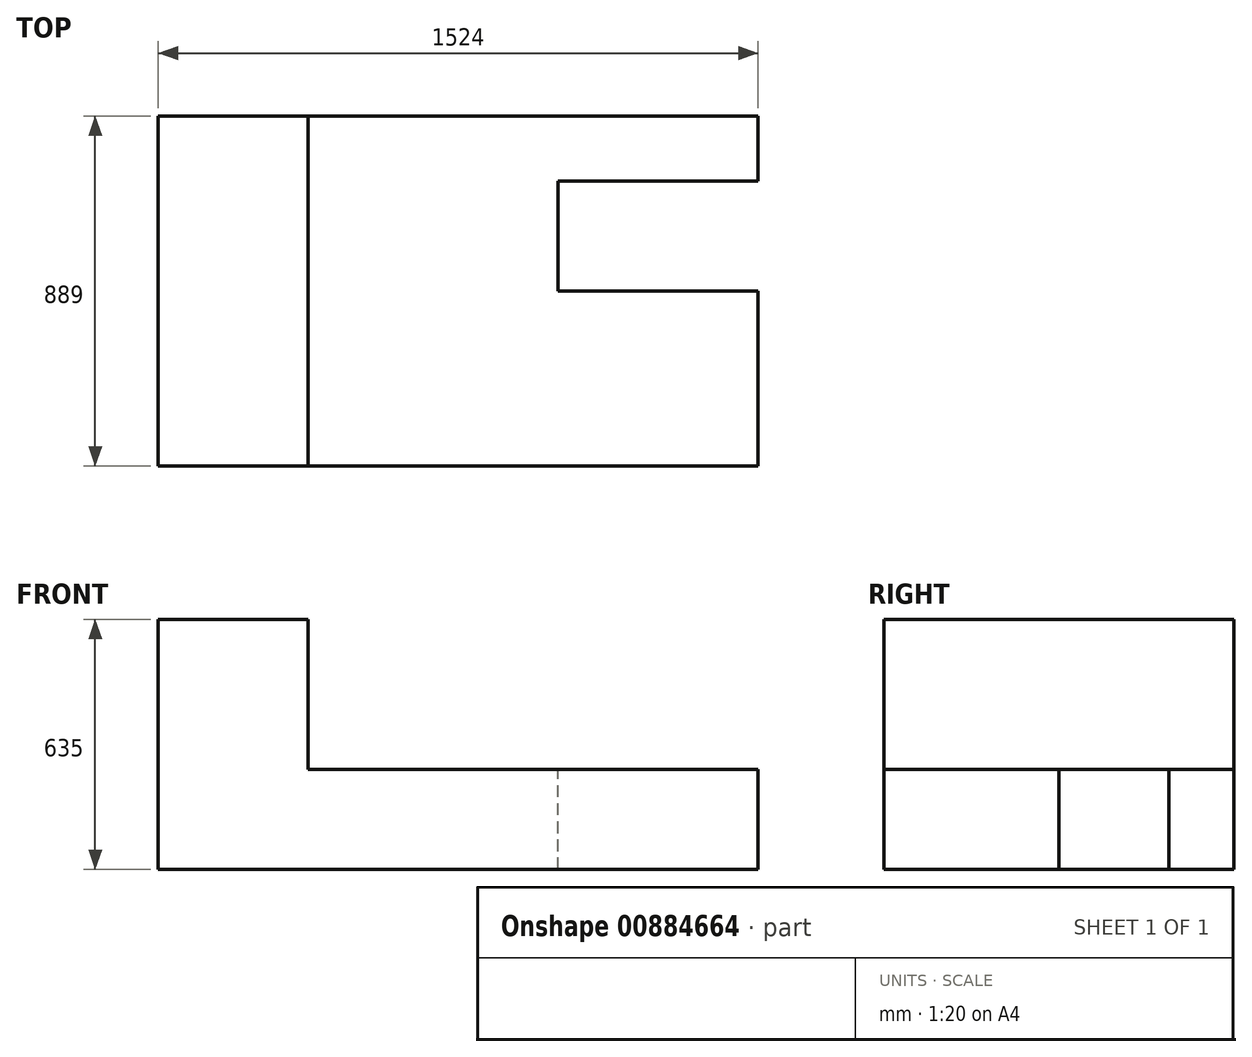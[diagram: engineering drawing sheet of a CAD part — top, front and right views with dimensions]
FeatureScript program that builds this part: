
annotation { "Feature Type Name" : "Feature", "Feature Type Description" : "" }
export const myFeature = defineFeature(function(context is Context, id is Id, definition is map)
    precondition{}
    {
        {
            var Q0;
            Q0=qCreatedBy(makeId("Front.planeOp"),FACE);
            var sketch = newSketch(context, id + "F0", { "sketchPlane" : qUnion([Q0])});
            skLineSegment(sketch, "E0", {"start": v(0, 0) * mm, "end": v(1524, 0) * mm});
            skLineSegment(sketch, "E1", {"start": v(1524, 0) * mm, "end": v(1524, 254) * mm});
            skLineSegment(sketch, "E2", {"start": v(1524, 254) * mm, "end": v(381, 254) * mm});
            skLineSegment(sketch, "E3", {"start": v(381, 254) * mm, "end": v(381, 635) * mm});
            skLineSegment(sketch, "E4", {"start": v(381, 635) * mm, "end": v(0, 635) * mm});
            skLineSegment(sketch, "E5", {"start": v(0, 635) * mm, "end": v(0, 0) * mm});
            skSolve(sketch);
        }
        {
            var Q0;
            Q0=makeQuery(id+"F0.imprint","IMPRINT",FACE,{"disambiguationData":[TD([[makeQuery(id+"F0.imprint","IMPRINT",EDGE,{"derivedFrom":sQuery(id+"F0.wireOp",EDGE,"E0")}),1.0]])]});
            extrude(context, id + "F1", {"entities" : qUnion([Q0]), "depth" : 889 * mm, "offsetDistance" : 25.4 * mm});
        }
        {
            var Q0;
            Q0=makeQuery(id+"F1.opExtrude","SWEPT_FACE",FACE,{"disambiguationData":[OSD([sQuery(id+"F0.wireOp",EDGE,"E2")])]});
            var sketch = newSketch(context, id + "F2", { "sketchPlane" : qUnion([Q0])});
            skLineSegment(sketch, "E6", {"start": v(1524, -444.5) * mm, "end": v(1016, -444.5) * mm});
            skLineSegment(sketch, "E7", {"start": v(1016, -444.5) * mm, "end": v(1016, -165.1) * mm});
            skLineSegment(sketch, "E8", {"start": v(1016, -165.1) * mm, "end": v(1524, -165.1) * mm});
            skSolve(sketch);
        }
        {
            var Q0;
            {var subQ0=sQuery(id+"F2.wireOp",EDGE,"E6");Q0=makeQuery(id+"F2.imprint","IMPRINT",FACE,{"disambiguationData":[TD([[makeQuery(id+"F2.imprint","IMPRINT",EDGE,{"derivedFrom":subQ0}),-1.0]])]});}
            extrude(context, id + "F3", {"entities" : qUnion([Q0]), "operationType" : NewBodyOperationType.REMOVE, "endBound" : BoundingType.THROUGH_ALL, "oppositeDirection" : true, "depth" : 25.4 * mm, "offsetDistance" : 25.4 * mm});
        }
    });
